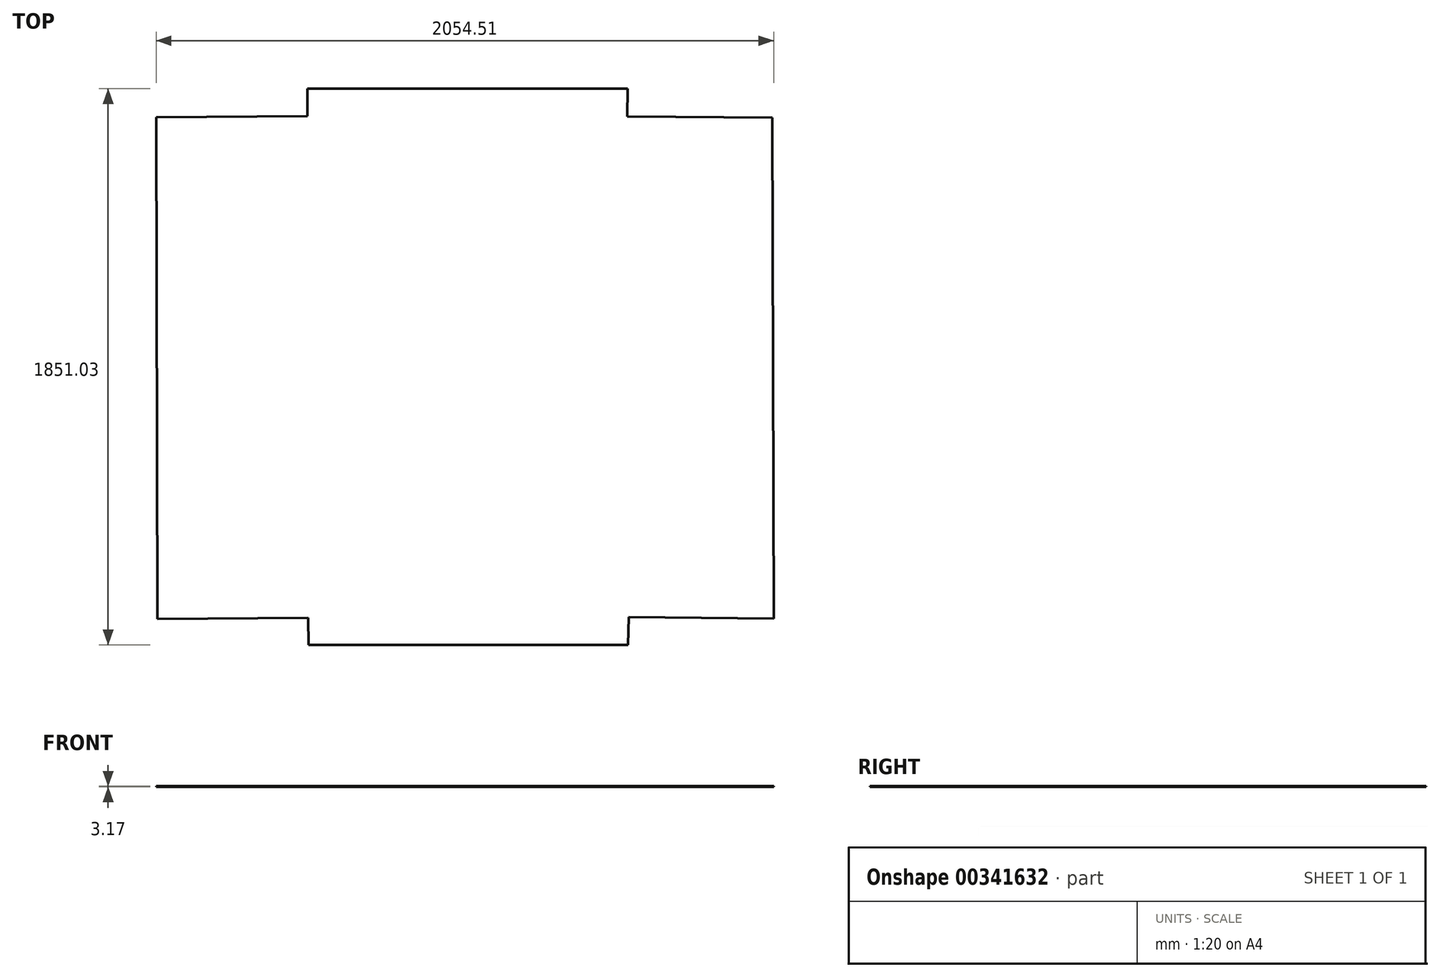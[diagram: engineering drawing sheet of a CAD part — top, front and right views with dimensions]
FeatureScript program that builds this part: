
annotation { "Feature Type Name" : "Feature", "Feature Type Description" : "" }
export const myFeature = defineFeature(function(context is Context, id is Id, definition is map)
    precondition{}
    {
        {
            var Q0;
            Q0=qCreatedBy(makeId("Top.planeOp"),FACE);
            var sketch = newSketch(context, id + "F0", { "sketchPlane" : qUnion([Q0])});
            skLineSegment(sketch, "E0", {"start": v(-537.46, 931.43) * mm, "end": v(530.93, 931.43) * mm});
            skLineSegment(sketch, "E1", {"start": v(-533.42, -922.77) * mm, "end": v(533.38, -922.77) * mm});
            skLineSegment(sketch, "E2", {"start": v(1012.74, 835.02) * mm, "end": v(1017.74, -835.02) * mm});
            skPoint(sketch, "E3", {"position": v(1015.24, 0) * mm});
            skLineSegment(sketch, "E4", {"start": v(-1039.96, 836.61) * mm, "end": v(-1036.77, -836.61) * mm});
            skPoint(sketch, "E5", {"position": v(-1038.36, 0) * mm});
            skLineSegment(sketch, "E6", {"start": v(-1039.96, 836.61) * mm, "end": v(-536.74, 840.95) * mm});
            skLineSegment(sketch, "E7", {"start": v(-536.74, 840.95) * mm, "end": v(-537.46, 931.43) * mm});
            skLineSegment(sketch, "E8", {"start": v(530.93, 931.43) * mm, "end": v(530.16, 839.36) * mm});
            skLineSegment(sketch, "E9", {"start": v(530.16, 839.36) * mm, "end": v(1012.74, 835.02) * mm});
            skLineSegment(sketch, "E10", {"start": v(1017.74, -835.02) * mm, "end": v(535.16, -830.7) * mm});
            skLineSegment(sketch, "E11", {"start": v(535.16, -830.7) * mm, "end": v(533.38, -922.77) * mm});
            skLineSegment(sketch, "E12", {"start": v(-533.42, -922.77) * mm, "end": v(-535.14, -832.3) * mm});
            skLineSegment(sketch, "E13", {"start": v(-535.14, -832.3) * mm, "end": v(-1036.77, -836.61) * mm});
            skSolve(sketch);
        }
        {
            var Q0;
            Q0=makeQuery(id+"F0.imprint","IMPRINT",FACE,{"disambiguationData":[TD([[makeQuery(id+"F0.imprint","IMPRINT",EDGE,{"derivedFrom":sQuery(id+"F0.wireOp",EDGE,"E0")}),-1.0]])]});
            var sketch = newSketch(context, id + "F1", { "sketchPlane" : qUnion([Q0])});
            skLineSegment(sketch, "E14.0", {"start": v(528.56, 837.79) * mm, "end": v(529.33, 929.85) * mm});
            skLineSegment(sketch, "E14.1", {"start": v(-1035.18, -835) * mm, "end": v(-533.58, -830.7) * mm});
            skLineSegment(sketch, "E14.2", {"start": v(-1038.36, 835.04) * mm, "end": v(-1035.18, -835) * mm});
            skLineSegment(sketch, "E14.3", {"start": v(-535.14, 839.38) * mm, "end": v(-1038.36, 835.04) * mm});
            skLineSegment(sketch, "E14.4", {"start": v(-535.86, 929.85) * mm, "end": v(-535.14, 839.38) * mm});
            skLineSegment(sketch, "E14.5", {"start": v(-533.58, -830.7) * mm, "end": v(-531.86, -921.18) * mm});
            skLineSegment(sketch, "E14.6", {"start": v(529.33, 929.85) * mm, "end": v(-535.86, 929.85) * mm});
            skLineSegment(sketch, "E14.7", {"start": v(-531.86, -921.18) * mm, "end": v(531.82, -921.18) * mm});
            skLineSegment(sketch, "E14.8", {"start": v(531.82, -921.18) * mm, "end": v(533.6, -829.1) * mm});
            skLineSegment(sketch, "E14.9", {"start": v(533.6, -829.1) * mm, "end": v(1016.15, -833.42) * mm});
            skLineSegment(sketch, "E14.10", {"start": v(1016.15, -833.42) * mm, "end": v(1011.16, 833.45) * mm});
            skLineSegment(sketch, "E14.11", {"start": v(1011.16, 833.45) * mm, "end": v(528.56, 837.79) * mm});
            skSolve(sketch);
        }
        {
            var Q0;
            Q0=qSketchRegion(id+"F1",true);
            extrude(context, id + "F2", {"entities" : qUnion([Q0]), "depth" : 3.17 * mm});
        }
    });
